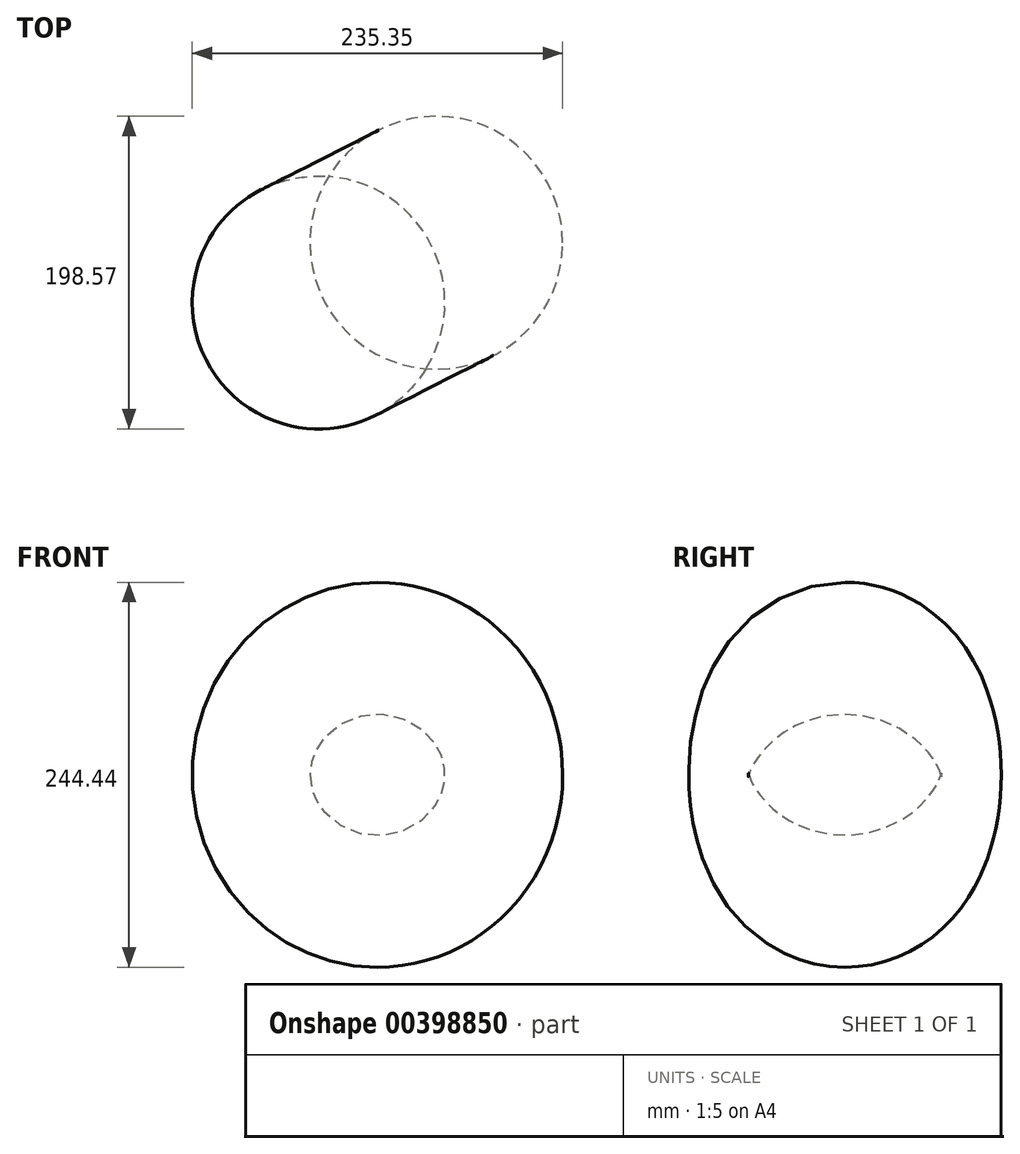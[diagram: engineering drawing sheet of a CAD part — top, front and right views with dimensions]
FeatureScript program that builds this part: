
annotation { "Feature Type Name" : "Feature", "Feature Type Description" : "" }
export const myFeature = defineFeature(function(context is Context, id is Id, definition is map)
    precondition{}
    {
        {
            var Q0;
            Q0=qCreatedBy(makeId("Top.planeOp"),FACE);
            var sketch = newSketch(context, id + "F0", { "sketchPlane" : qUnion([Q0])});
            skLineSegment(sketch, "E0", {"start": v(-5.3, 51.93) * mm, "end": v(56.73, -70.17) * mm});
            skArc(sketch, "E1", {"start": v(-5.3, 51.93) * mm, "mid": v(-8.5, -26.5) * mm, "end": v(56.73, -70.17) * mm});
            skSolve(sketch);
        }
        {
            var Q0;
            Q0=makeQuery(id+"F0.imprint","IMPRINT",FACE,{"disambiguationData":[TD([[makeQuery(id+"F0.imprint","IMPRINT",EDGE,{"derivedFrom":sQuery(id+"F0.wireOp",EDGE,"E0")}),-1.0]])]});
            var Q1;
            Q1=sQuery(id+"F0.wireOp",EDGE,"E0");
            revolve(context, id + "F1", {"entities" : qUnion([Q0]), "axis" : qUnion([Q1]), "revolveType" : RevolveType.ONE_DIRECTION, "oppositeDirection" : true, "angle" : 360 * degree});
        }
    });
